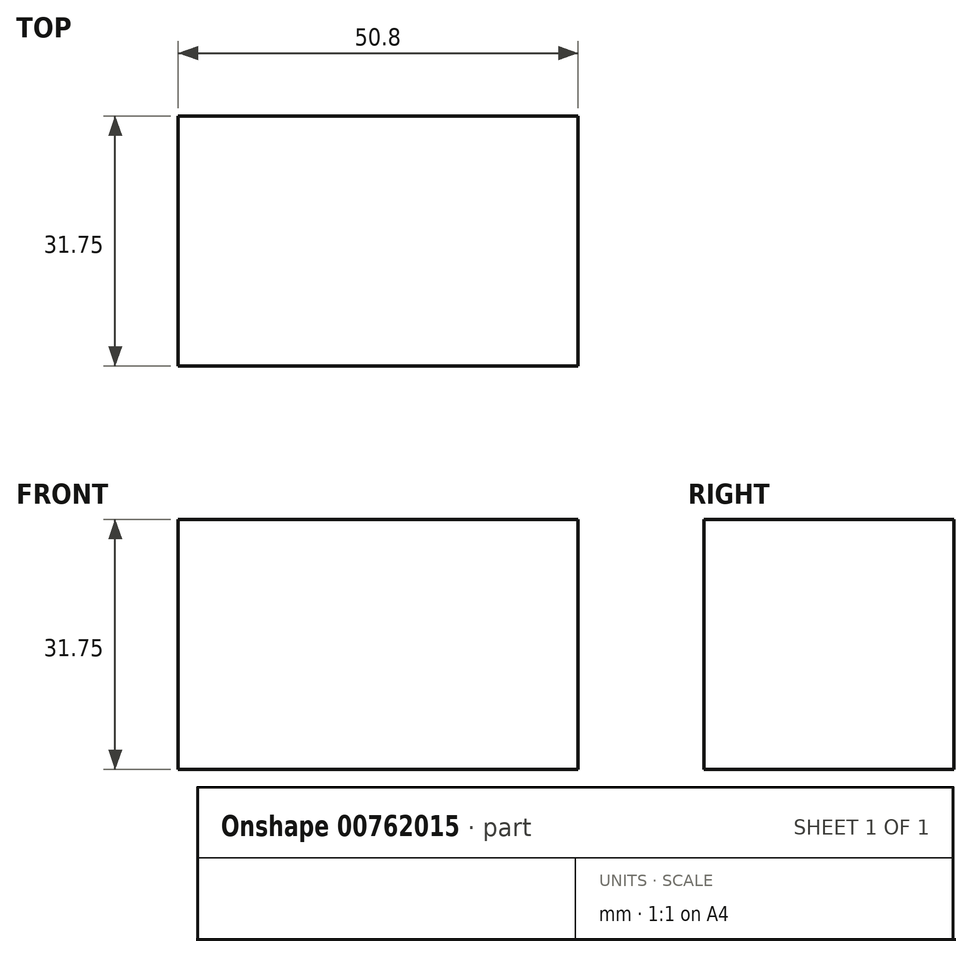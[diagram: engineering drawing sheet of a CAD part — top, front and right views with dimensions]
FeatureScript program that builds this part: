
annotation { "Feature Type Name" : "Feature", "Feature Type Description" : "" }
export const myFeature = defineFeature(function(context is Context, id is Id, definition is map)
    precondition{}
    {
        {
            var Q0;
            Q0=qCreatedBy(makeId("Front.planeOp"),FACE);
            var sketch = newSketch(context, id + "F0", { "sketchPlane" : qUnion([Q0])});
            skLineSegment(sketch, "E0", {"start": v(0, 0) * mm, "end": v(0, 31.75) * mm});
            skLineSegment(sketch, "E1", {"start": v(0, 31.75) * mm, "end": v(50.8, 31.75) * mm});
            skLineSegment(sketch, "E2", {"start": v(50.8, 31.75) * mm, "end": v(50.8, 0) * mm});
            skLineSegment(sketch, "E3", {"start": v(50.8, 0) * mm, "end": v(0, 0) * mm});
            skSolve(sketch);
        }
        {
            var Q0;
            Q0 = qSketchRegion(id + "F0", true);
            extrude(context, id + "F1", {"entities" : qUnion([Q0]), "depth" : 31.75 * mm, "offsetDistance" : 25.4 * mm});
        }
    });
